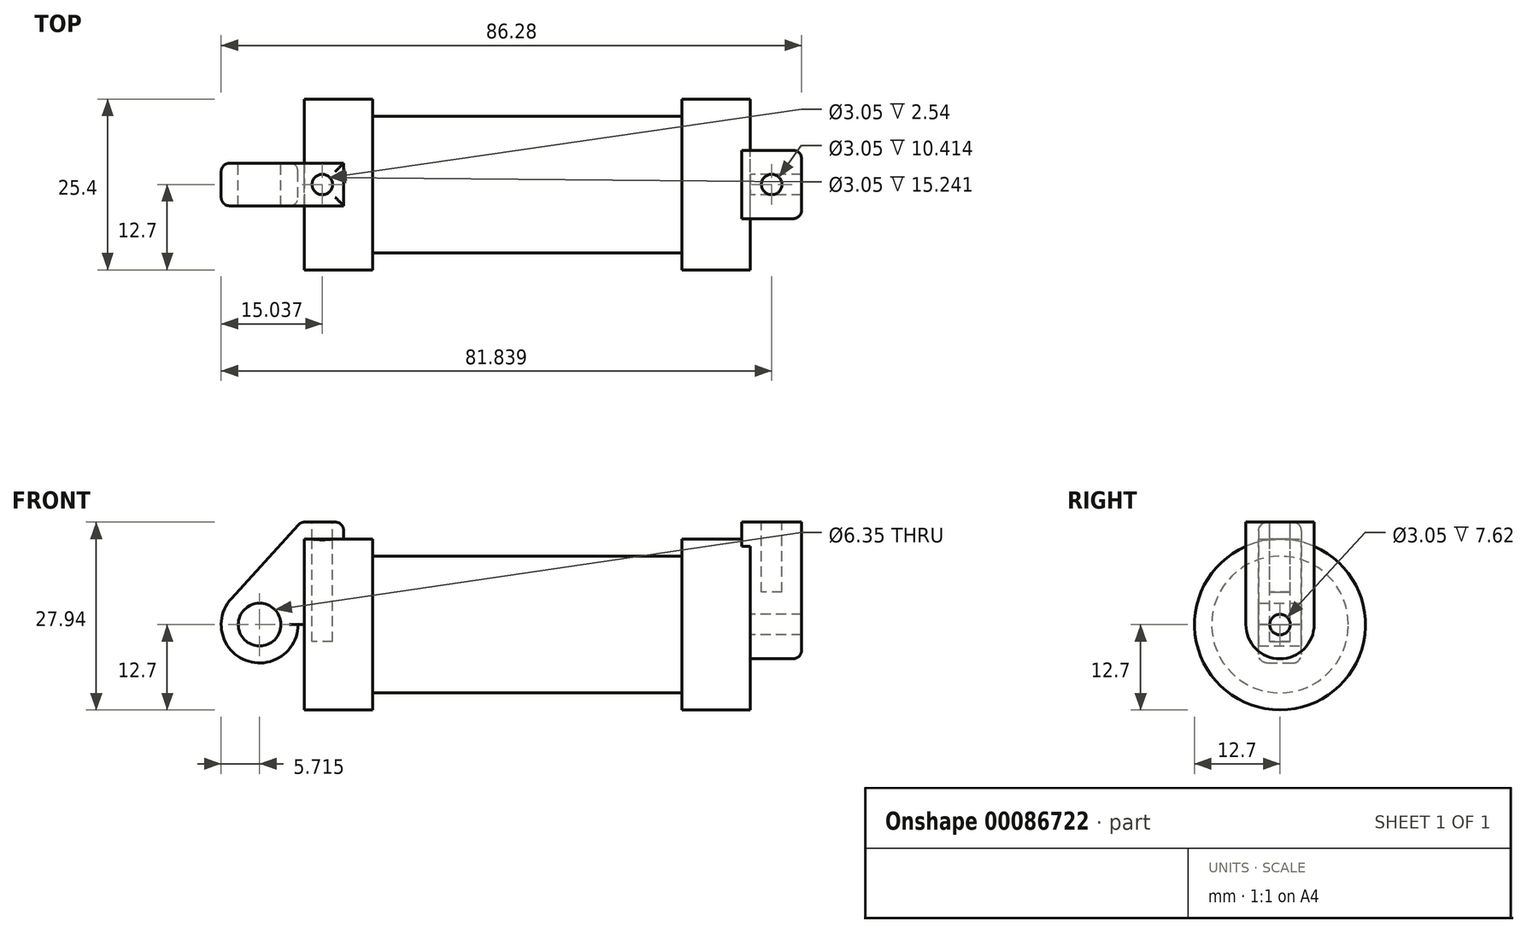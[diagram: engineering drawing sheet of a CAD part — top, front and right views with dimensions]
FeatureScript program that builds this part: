
annotation { "Feature Type Name" : "Feature", "Feature Type Description" : "" }
export const myFeature = defineFeature(function(context is Context, id is Id, definition is map)
    precondition{}
    {
        {
            var Q0;
            Q0=qCreatedBy(makeId("Front.planeOp"),FACE);
            var sketch = newSketch(context, id + "F0", { "sketchPlane" : qUnion([Q0])});
            skLineSegment(sketch, "E0", {"start": v(0, 0) * mm, "end": v(0, 12.7) * mm});
            skLineSegment(sketch, "E1", {"start": v(0, 12.7) * mm, "end": v(10.16, 12.7) * mm});
            skLineSegment(sketch, "E2", {"start": v(10.16, 12.7) * mm, "end": v(10.16, 10.16) * mm});
            skLineSegment(sketch, "E3", {"start": v(10.16, 10.16) * mm, "end": v(56.13, 10.16) * mm});
            skLineSegment(sketch, "E4", {"start": v(56.13, 10.16) * mm, "end": v(56.13, 12.7) * mm});
            skLineSegment(sketch, "E5", {"start": v(56.13, 12.7) * mm, "end": v(66.3, 12.7) * mm});
            skLineSegment(sketch, "E6", {"start": v(66.3, 12.7) * mm, "end": v(66.3, 0) * mm});
            skLineSegment(sketch, "E7", {"start": v(66.3, 0) * mm, "end": v(0, 0) * mm});
            skLineSegment(sketch, "E8", {"start": v(5.84, 15.24) * mm, "end": v(-0.5, 15.24) * mm});
            skLineSegment(sketch, "E9", {"start": v(-0.5, 15.24) * mm, "end": v(-10.88, 3.85) * mm});
            skLineSegment(sketch, "E10", {"start": v(0, 0) * mm, "end": v(-6.65, 0) * mm});
            skCircle(sketch, "E11", {"center": v(-6.65, 0) * mm, "radius": 5.72 * mm});
            skCircle(sketch, "E12", {"center": v(-6.65, 0) * mm, "radius": 3.18 * mm});
            skLineSegment(sketch, "E13", {"start": v(5.84, 15.24) * mm, "end": v(5.84, -9.4) * mm});
            skLineSegment(sketch, "E14", {"start": v(5.84, -9.4) * mm, "end": v(-8.18, -5.5) * mm});
            skSolve(sketch);
        }
        {
            var Q0;
            {var subQ0=sQuery(id+"F0.wireOp",EDGE,"E2");Q0=makeQuery(id+"F0.imprint","IMPRINT",FACE,{"disambiguationData":[TD([[makeQuery(id+"F0.imprint","IMPRINT",EDGE,{"derivedFrom":subQ0}),-1.0]])]});}
            var Q1;
            {var subQ0=sQuery(id+"F0.wireOp",EDGE,"E0");Q1=makeQuery(id+"F0.imprint","IMPRINT",FACE,{"disambiguationData":[TD([[makeQuery(id+"F0.imprint","IMPRINT",EDGE,{"derivedFrom":subQ0}),-1.0]])]});}
            var Q2;
            Q2=sQuery(id+"F0.wireOp",EDGE,"E7");
            revolve(context, id + "F1", {"entities" : qUnion([Q0, Q1]), "axis" : qUnion([Q2]), "revolveType" : RevolveType.FULL});
        }
        {
            var Q0;
            {var subQ3=sQuery(id+"F0.wireOp",EDGE,"E0");Q0=makeQuery(id+"F0.imprint","IMPRINT",FACE,{"disambiguationData":[TD([[makeQuery(id+"F0.imprint","IMPRINT",EDGE,{"derivedFrom":subQ3}),1.0]])]});}
            var Q1;
            {var subQ4=sQuery(id+"F0.wireOp",EDGE,"E12");Q1=makeQuery(id+"F0.imprint","IMPRINT",FACE,{"disambiguationData":[TD([[makeQuery(id+"F0.imprint","IMPRINT",EDGE,{"derivedFrom":subQ4}),-1.0]])]});}
            extrude(context, id + "F2", {"entities" : qUnion([Q0, Q1]), "endBound" : BoundingType.SYMMETRIC, "depth" : 6.35 * mm});
        }
        {
            var Q0;
            Q0=makeQuery(id+"F1.opRevolve","SWEPT_FACE",FACE,{"disambiguationData":[OSD([sQuery(id+"F0.wireOp",EDGE,"E6")])]});
            var sketch = newSketch(context, id + "F3", { "sketchPlane" : qUnion([Q0])});
            skCircle(sketch, "E15", {"center": v(0, 0) * mm, "radius": 1.52 * mm});
            skCircle(sketch, "E16", {"center": v(0, 0) * mm, "radius": 5.08 * mm});
            skLineSegment(sketch, "E17", {"start": v(5.08, 0) * mm, "end": v(5.08, 15.24) * mm});
            skLineSegment(sketch, "E18", {"start": v(-5.08, 0) * mm, "end": v(-5.08, 15.24) * mm});
            skLineSegment(sketch, "E19", {"start": v(-5.08, 15.24) * mm, "end": v(5.08, 15.24) * mm});
            skSolve(sketch);
        }
        {
            var Q0;
            Q0 = qSketchRegion(id + "F3", true);
            extrude(context, id + "F4", {"entities" : qUnion([Q0]), "operationType" : NewBodyOperationType.ADD, "depth" : 7.62 * mm});
        }
        {
            var Q0;
            Q0 = qSketchRegion(id + "F3", true);
            extrude(context, id + "F5", {"entities" : qUnion([Q0]), "operationType" : NewBodyOperationType.ADD, "oppositeDirection" : true, "depth" : 1.27 * mm});
        }
        {
            var Q0;
            {var subQ0=sQuery(id+"F3.wireOp",EDGE,"E19");Q0=makeQuery(id+"F5.boolean.opBoolean","MERGE",FACE,{"derivedFrom":[makeQuery(id+"F4.opExtrude","SWEPT_FACE",FACE,{"disambiguationData":[OSD([subQ0])]}),makeQuery(id+"F5.opExtrude","SWEPT_FACE",FACE,{"disambiguationData":[OSD([subQ0])]})]});}
            var sketch = newSketch(context, id + "F6", { "sketchPlane" : qUnion([Q0])});
            skLineSegment(sketch, "E20", {"start": v(65.02, 5.08) * mm, "end": v(73.91, -5.08) * mm, "construction": true});
            skCircle(sketch, "E21", {"center": v(69.47, 0) * mm, "radius": 1.52 * mm});
            skSolve(sketch);
        }
        {
            var Q0;
            Q0=makeQuery(id+"F6.imprint","IMPRINT",FACE,{"disambiguationData":[TD([[makeQuery(id+"F6.imprint","IMPRINT",EDGE,{"derivedFrom":sQuery(id+"F6.wireOp",EDGE,"E21")}),1.0]])]});
            var Q1;
            Q1=sQuery(id+"F6.wireOp",EDGE,"E21");
            extrude(context, id + "F7", {"entities" : qUnion([Q0]), "operationType" : NewBodyOperationType.REMOVE, "surfaceEntities" : qUnion([Q1]), "oppositeDirection" : true, "depth" : 10.4 * mm});
        }
        {
            var Q0;
            Q0=makeQuery(id+"F2.opExtrude","SWEPT_FACE",FACE,{"disambiguationData":[OSD([sQuery(id+"F0.wireOp",EDGE,"E8")])]});
            var sketch = newSketch(context, id + "F8", { "sketchPlane" : qUnion([Q0])});
            skCircle(sketch, "E22", {"center": v(2.67, 0) * mm, "radius": 1.52 * mm});
            skPoint(sketch, "E22.centerSnap0", {"position": v(2.67, 3.18) * mm});
            skPoint(sketch, "E22.centerSnap1", {"position": v(-0.5, 0) * mm});
            skSolve(sketch);
        }
        {
            var Q0;
            Q0 = qSketchRegion(id + "F8", true);
            extrude(context, id + "F9", {"entities" : qUnion([Q0]), "operationType" : NewBodyOperationType.REMOVE, "oppositeDirection" : true, "depth" : 17.78 * mm});
        }
        {
            var Q0;
            Q0=makeQuery(id+"F2.opExtrude","CAP_EDGE",EDGE,{"disambiguationData":[OSD([sQuery(id+"F0.wireOp",EDGE,"E8")])],"isStart":true});
            var Q1;
            Q1=makeQuery(id+"F2.opExtrude","SWEPT_EDGE",EDGE,{"disambiguationData":[OSD([sQuery(id+"F0.wireOp",EDGE,"E8"),sQuery(id+"F0.wireOp",EDGE,"E13")])]});
            var Q2;
            Q2=makeQuery(id+"F2.opExtrude","SWEPT_EDGE",EDGE,{"disambiguationData":[OSD([sQuery(id+"F0.wireOp",EDGE,"E8"),sQuery(id+"F0.wireOp",EDGE,"E9")])]});
            var Q3;
            Q3=makeQuery(id+"F2.opExtrude","CAP_EDGE",EDGE,{"disambiguationData":[OSD([sQuery(id+"F0.wireOp",EDGE,"E8")])],"isStart":false});
            var Q4;
            Q4=makeQuery(id+"F2.opExtrude","CAP_EDGE",EDGE,{"disambiguationData":[OSD([sQuery(id+"F0.wireOp",EDGE,"E9")])],"isStart":false});
            var Q5;
            Q5=makeQuery(id+"F2.opExtrude","CAP_EDGE",EDGE,{"disambiguationData":[OSD([sQuery(id+"F0.wireOp",EDGE,"E9")])],"isStart":true});
            var Q6;
            Q6=makeQuery(id+"F2.opExtrude","CAP_EDGE",EDGE,{"disambiguationData":[OSD([sQuery(id+"F0.wireOp",EDGE,"E11")])],"isStart":false});
            var Q7;
            Q7=makeQuery(id+"F2.opExtrude","CAP_EDGE",EDGE,{"disambiguationData":[OSD([sQuery(id+"F0.wireOp",EDGE,"E11")])],"isStart":true});
            var Q8;
            Q8=makeQuery(id+"F1.opRevolve","SWEPT_EDGE",EDGE,{"disambiguationData":[OSD([sQuery(id+"F0.wireOp",EDGE,"E4"),sQuery(id+"F0.wireOp",EDGE,"E5")])]});
            var Q9;
            Q9=makeQuery(id+"F4.boolean.opBoolean","SPLIT",EDGE,{"disambiguationData":[OD(1.0)],"derivedFrom":makeQuery(id+"F1.opRevolve","SWEPT_EDGE",EDGE,{"disambiguationData":[OSD([sQuery(id+"F0.wireOp",EDGE,"E5"),sQuery(id+"F0.wireOp",EDGE,"E6")])]})});
            var Q10;
            Q10=makeQuery(id+"F1.opRevolve","SWEPT_EDGE",EDGE,{"disambiguationData":[OSD([sQuery(id+"F0.wireOp",EDGE,"E1"),sQuery(id+"F0.wireOp",EDGE,"E2")])]});
            var Q11;
            Q11=makeQuery(id+"F1.opRevolve","SWEPT_EDGE",EDGE,{"disambiguationData":[OSD([sQuery(id+"F0.wireOp",EDGE,"E0"),sQuery(id+"F0.wireOp",EDGE,"E1")])]});
            var Q12;
            {var subQ0=sQuery(id+"F3.wireOp",EDGE,"E19");var subQ1=sQuery(id+"F3.wireOp",EDGE,"E17");Q12=makeQuery(id+"F5.boolean.opBoolean","MERGE",EDGE,{"derivedFrom":[makeQuery(id+"F4.opExtrude","SWEPT_EDGE",EDGE,{"disambiguationData":[OSD([subQ1,subQ0])]}),makeQuery(id+"F5.opExtrude","SWEPT_EDGE",EDGE,{"disambiguationData":[OSD([subQ1,subQ0])]})]});}
            var Q13;
            Q13=makeQuery(id+"F5.opExtrude","CAP_EDGE",EDGE,{"disambiguationData":[OSD([sQuery(id+"F3.wireOp",EDGE,"E19")])],"isStart":false});
            var Q14;
            Q14=makeQuery(id+"F4.opExtrude","CAP_EDGE",EDGE,{"disambiguationData":[OSD([sQuery(id+"F3.wireOp",EDGE,"E19")])],"isStart":false});
            var Q15;
            {var subQ0=sQuery(id+"F3.wireOp",EDGE,"E19");var subQ1=sQuery(id+"F3.wireOp",EDGE,"E18");Q15=makeQuery(id+"F5.boolean.opBoolean","MERGE",EDGE,{"derivedFrom":[makeQuery(id+"F4.opExtrude","SWEPT_EDGE",EDGE,{"disambiguationData":[OSD([subQ1,subQ0])]}),makeQuery(id+"F5.opExtrude","SWEPT_EDGE",EDGE,{"disambiguationData":[OSD([subQ1,subQ0])]})]});}
            var Q16;
            Q16=makeQuery(id+"F5.boolean.opBoolean","INTERSECT",EDGE,{"derivedFrom":[makeQuery(id+"F1.opRevolve","SWEPT_FACE",FACE,{"disambiguationData":[OSD([sQuery(id+"F0.wireOp",EDGE,"E5")])]}),makeQuery(id+"F5.opExtrude","SWEPT_FACE",FACE,{"disambiguationData":[OSD([sQuery(id+"F3.wireOp",EDGE,"E18")])]})]});
            var Q17;
            Q17=makeQuery(id+"F5.opExtrude","CAP_EDGE",EDGE,{"disambiguationData":[OSD([sQuery(id+"F3.wireOp",EDGE,"E18")])],"isStart":false});
            var Q18;
            Q18=makeQuery(id+"F5.opExtrude","CAP_EDGE",EDGE,{"disambiguationData":[OSD([sQuery(id+"F3.wireOp",EDGE,"E17")])],"isStart":false});
            var Q19;
            Q19=makeQuery(id+"F5.boolean.opBoolean","INTERSECT",EDGE,{"derivedFrom":[makeQuery(id+"F1.opRevolve","SWEPT_FACE",FACE,{"disambiguationData":[OSD([sQuery(id+"F0.wireOp",EDGE,"E5")])]}),makeQuery(id+"F5.opExtrude","CAP_FACE",FACE,{"disambiguationData":[OSD([sQuery(id+"F3.wireOp",EDGE,"E15"),sQuery(id+"F3.wireOp",EDGE,"E16"),sQuery(id+"F3.wireOp",EDGE,"E17"),sQuery(id+"F3.wireOp",EDGE,"E18"),sQuery(id+"F3.wireOp",EDGE,"E19")])],"isStart":false})]});
            fillet(context, id + "F10", {"entities" : qUnion([Q0, Q1, Q2, Q3, Q4, Q5, Q6, Q7, Q8, Q9, Q10, Q11, Q12, Q13, Q14, Q15, Q16, Q17, Q18, Q19]), "radius" : 1.27 * mm, "tangentPropagation" : true, "allowEdgeOverflow" : false});
        }
        {
            var Q0;
            Q0=makeQuery(id+"F4.opExtrude","CAP_EDGE",EDGE,{"disambiguationData":[OSD([sQuery(id+"F3.wireOp",EDGE,"E17")])],"isStart":false});
            var Q1;
            {var subQ0=sQuery(id+"F0.wireOp",EDGE,"E0");Q1=makeQuery(id+"F10.opFillet","BLEND_EDGE",EDGE,{"blendedFrom":[makeQuery(id+"F1.opRevolve","SWEPT_EDGE",EDGE,{"disambiguationData":[OSD([subQ0,sQuery(id+"F0.wireOp",EDGE,"E1")])]}),makeQuery(id+"F1.opRevolve","SWEPT_FACE",FACE,{"disambiguationData":[OSD([subQ0])]})],"blendedInto":[makeQuery(id+"F1.opRevolve","SWEPT_FACE",FACE,{"disambiguationData":[OSD([subQ0])]})]});}
            fillet(context, id + "F11", {"entities" : qUnion([Q0, Q1]), "radius" : 1.27 * mm, "tangentPropagation" : true, "allowEdgeOverflow" : false});
        }
    });
